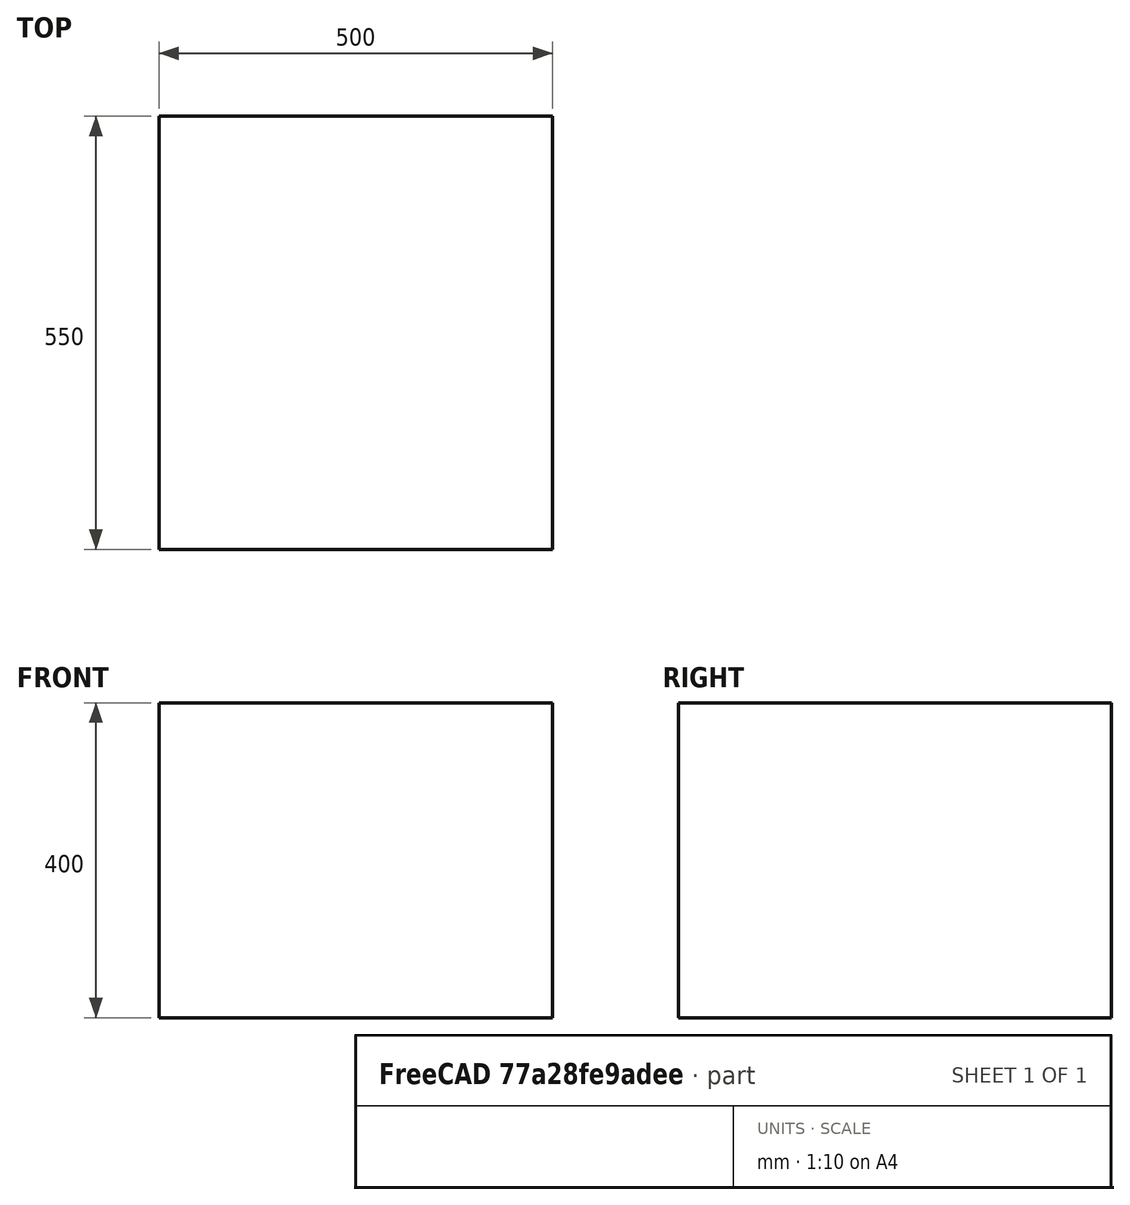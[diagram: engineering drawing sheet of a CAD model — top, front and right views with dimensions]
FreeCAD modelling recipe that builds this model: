
FCSTD DOCUMENT  (FreeCAD 0.21RUnknown)
Label: prusa-box
License: All rights reserved
LicenseURL: http://en.wikipedia.org/wiki/All_rights_reserved
objects: Sketcher::SketchObject×1, PartDesign::Pad×1, PartDesign::Body×1, Spreadsheet::Sheet×1
note: 4 computed .brp shape members not serialized (recipe doc carries the construction recipe); baked Part::Feature solids carry a one-line shape summary decoded from their .brp

FEATURE [Sketcher::SketchObject] Sketch
  FullyConstrained = true
  MapMode = 5
  Support = -> [XY_Plane]
  expr: Constraints[10] = <<MK3+>>.printer_width
  expr: Constraints[11] = <<MK3+>>.printer_length
  sketch-geometry (5):
    g0: LineSegment StartX=250 StartY=-275 StartZ=0 EndX=250 EndY=275 EndZ=0
    g1: LineSegment StartX=250 StartY=275 StartZ=0 EndX=-250 EndY=275 EndZ=0
    g2: LineSegment StartX=-250 StartY=275 StartZ=0 EndX=-250 EndY=-275 EndZ=0
    g3: LineSegment StartX=-250 StartY=-275 StartZ=0 EndX=250 EndY=-275 EndZ=0
    g4: GeomPoint X=0 Y=0 Z=0
  constraints (12):
    c: Coincident(g0,g1)
    c: Coincident(g1,g2)
    c: Coincident(g2,g3)
    c: Coincident(g3,g0)
    c: Horizontal(g1)
    c: Horizontal(g3)
    c: Vertical(g0)
    c: Vertical(g2)
    c: Symmetric(g1,g0,g4)
    c: Coincident(g4,g-1)
    c: DistanceX(g1,g1) = 500
    c: DistanceY(g2,g2) = 550
FEATURE [PartDesign::Pad] Pad
  Direction = (0,0,1)
  Length = 400
  Length2 = 10
  Profile = -> Sketch
  ReferenceAxis = -> Sketch [N_Axis]
  Type = 0
FEATURE [PartDesign::Body] Body
  Group = -> [Sketch,Pad]
  Origin = -> Origin
  Tip = -> Pad
FEATURE [Spreadsheet::Sheet] Spreadsheet  label="MK3+"
  cells = A1='Length; B1='Width; C1='Height; D1='Filament Spool (Coservative); A2(printer_length)=550; B2(printer_width)=500; C2(printer_height)=400; D2(spool_height_conservative)=300
